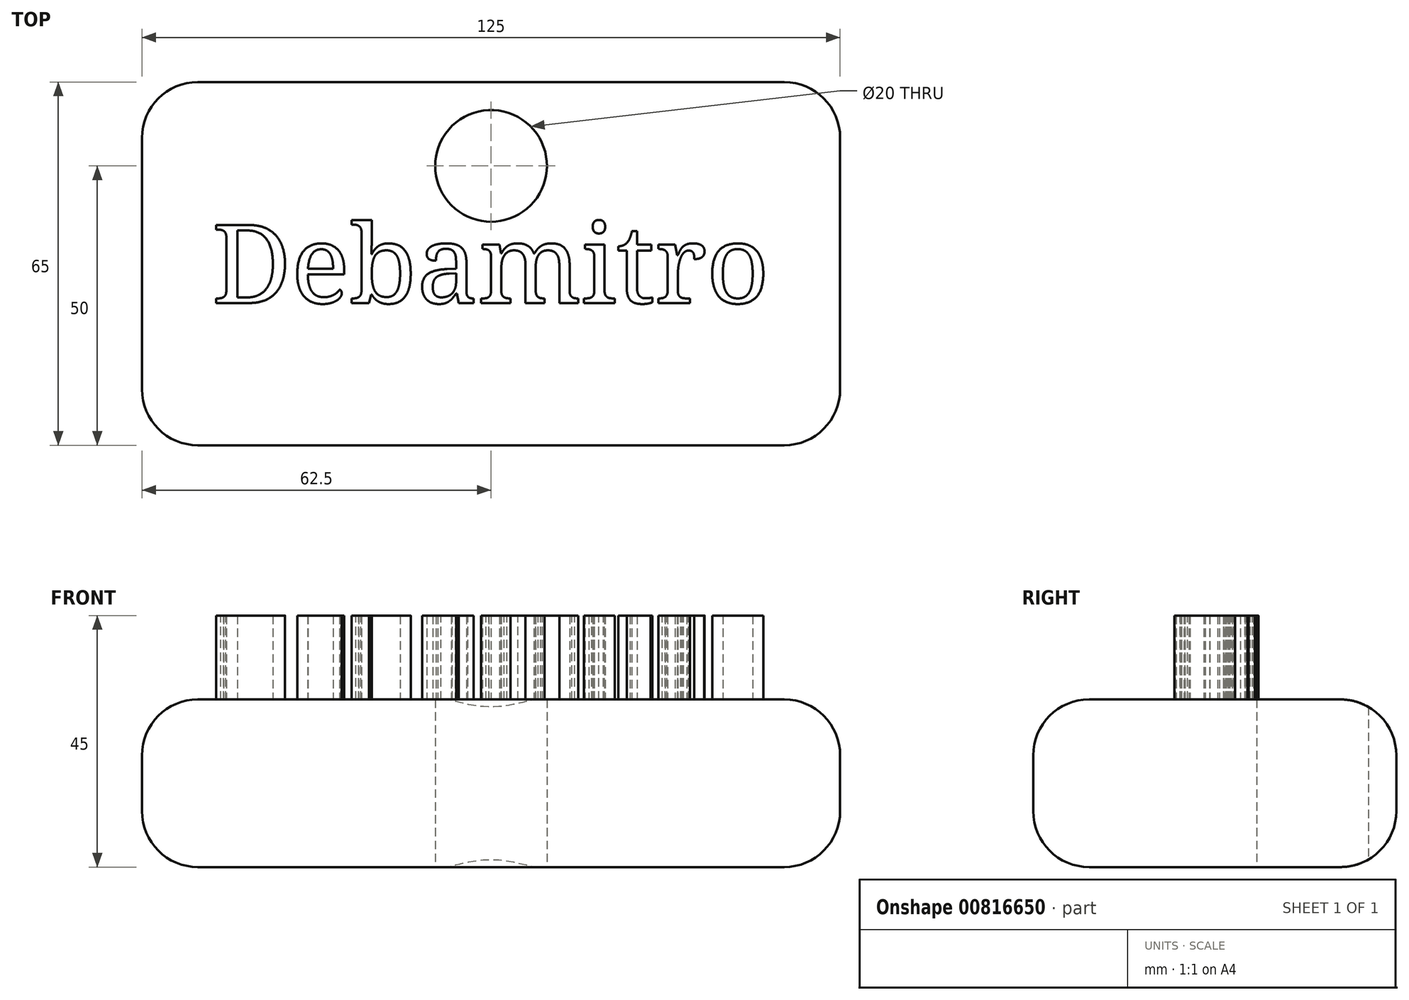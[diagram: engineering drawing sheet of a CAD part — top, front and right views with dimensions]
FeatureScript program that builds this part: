
annotation { "Feature Type Name" : "Feature", "Feature Type Description" : "" }
export const myFeature = defineFeature(function(context is Context, id is Id, definition is map)
    precondition{}
    {
        {
            var Q0;
            Q0=qCreatedBy(makeId("Top.planeOp"),FACE);
            var sketch = newSketch(context, id + "F0", { "sketchPlane" : qUnion([Q0])});
            skLineSegment(sketch, "E0.bottom", {"start": v(62.5, -32.5) * mm, "end": v(-62.5, -32.5) * mm});
            skLineSegment(sketch, "E0.top", {"start": v(62.5, 32.5) * mm, "end": v(-62.5, 32.5) * mm});
            skLineSegment(sketch, "E0.left", {"start": v(62.5, -32.5) * mm, "end": v(62.5, 32.5) * mm});
            skLineSegment(sketch, "E0.right", {"start": v(-62.5, -32.5) * mm, "end": v(-62.5, 32.5) * mm});
            skPoint(sketch, "E0.middle", {"position": v(0, 0) * mm});
            skSolve(sketch);
        }
        {
            var Q0;
            Q0=makeQuery(id+"F0.imprint","IMPRINT",FACE,{"disambiguationData":[TD([[makeQuery(id+"F0.imprint","IMPRINT",EDGE,{"derivedFrom":sQuery(id+"F0.wireOp",EDGE,"E0.bottom")}),-1.0]])]});
            extrude(context, id + "F1", {"entities" : qUnion([Q0]), "depth" : 30 * mm, "offsetDistance" : 25 * mm});
        }
        {
            var Q0;
            Q0=makeQuery(id+"F1.opExtrude","CAP_FACE",FACE,{"disambiguationData":[OSD([sQuery(id+"F0.wireOp",EDGE,"E0.bottom"),sQuery(id+"F0.wireOp",EDGE,"E0.top"),sQuery(id+"F0.wireOp",EDGE,"E0.left"),sQuery(id+"F0.wireOp",EDGE,"E0.right")])],"isStart":false});
            var sketch = newSketch(context, id + "F2", { "sketchPlane" : qUnion([Q0])});
            skText(sketch, "E1", { "text": "Debamitro", "fontName": "NotoSerif-Regular.ttf"});
            skLineSegment(sketch, "E2", {"start": v(0, 7.04) * mm, "end": v(0, 37.53) * mm, "construction": true});
            skLineSegment(sketch, "E3", {"start": v(-50, 0) * mm, "end": v(-58.74, 0) * mm, "construction": true});
            skLineSegment(sketch, "E4", {"start": v(-58.74, 0) * mm, "end": v(-58.48, 1.44) * mm});
            skLineSegment(sketch, "E5", {"start": v(0, -7.04) * mm, "end": v(0, -32.63) * mm, "construction": true});
            skLineSegment(sketch, "E6", {"start": v(50, 0) * mm, "end": v(63.06, 0) * mm, "construction": true});
            const initialGuessF2  = {"E1": [-0.05, -0.00704, 1, 0, 0.01408]};
            skSetInitialGuess(sketch, initialGuessF2);
            skSolve(sketch);
        }
        {
            var Q0;
            Q0 = qSketchRegion(id + "F2", true);
            extrude(context, id + "F3", {"entities" : qUnion([Q0]), "operationType" : NewBodyOperationType.ADD, "depth" : 15 * mm, "offsetDistance" : 25 * mm});
        }
        {
            var Q0;
            Q0=qCreatedBy(makeId("Top.planeOp"),FACE);
            var sketch = newSketch(context, id + "F4", { "sketchPlane" : qUnion([Q0])});
            skCircle(sketch, "E7", {"center": v(0, 17.5) * mm, "radius": 10 * mm});
            skLineSegment(sketch, "E8", {"start": v(0, 17.5) * mm, "end": v(0, 17.5) * mm});
            skLineSegment(sketch, "E9", {"start": v(0, 17.5) * mm, "end": v(0, 32.5) * mm});
            skSolve(sketch);
        }
        {
            var Q0;
            Q0 = qSketchRegion(id + "F4", true);
            extrude(context, id + "F5", {"entities" : qUnion([Q0]), "operationType" : NewBodyOperationType.REMOVE, "depth" : 59 * mm, "offsetDistance" : 25 * mm});
        }
        {
            var Q0;
            Q0=makeQuery(id+"F1.opExtrude","CAP_EDGE",EDGE,{"disambiguationData":[OSD([sQuery(id+"F0.wireOp",EDGE,"E0.right")])],"isStart":false});
            var Q1;
            Q1=makeQuery(id+"F1.opExtrude","CAP_EDGE",EDGE,{"disambiguationData":[OSD([sQuery(id+"F0.wireOp",EDGE,"E0.right")])],"isStart":true});
            var Q2;
            Q2=makeQuery(id+"F1.opExtrude","CAP_EDGE",EDGE,{"disambiguationData":[OSD([sQuery(id+"F0.wireOp",EDGE,"E0.top")])],"isStart":false});
            var Q3;
            Q3=makeQuery(id+"F1.opExtrude","CAP_EDGE",EDGE,{"disambiguationData":[OSD([sQuery(id+"F0.wireOp",EDGE,"E0.top")])],"isStart":true});
            var Q4;
            Q4=makeQuery(id+"F1.opExtrude","CAP_EDGE",EDGE,{"disambiguationData":[OSD([sQuery(id+"F0.wireOp",EDGE,"E0.left")])],"isStart":false});
            var Q5;
            Q5=makeQuery(id+"F1.opExtrude","CAP_EDGE",EDGE,{"disambiguationData":[OSD([sQuery(id+"F0.wireOp",EDGE,"E0.bottom")])],"isStart":false});
            var Q6;
            Q6=makeQuery(id+"F1.opExtrude","SWEPT_EDGE",EDGE,{"disambiguationData":[OSD([sQuery(id+"F0.wireOp",EDGE,"E0.bottom"),sQuery(id+"F0.wireOp",EDGE,"E0.right")])]});
            var Q7;
            Q7=makeQuery(id+"F1.opExtrude","SWEPT_EDGE",EDGE,{"disambiguationData":[OSD([sQuery(id+"F0.wireOp",EDGE,"E0.bottom"),sQuery(id+"F0.wireOp",EDGE,"E0.left")])]});
            var Q8;
            Q8=makeQuery(id+"F1.opExtrude","CAP_EDGE",EDGE,{"disambiguationData":[OSD([sQuery(id+"F0.wireOp",EDGE,"E0.left")])],"isStart":true});
            var Q9;
            Q9=makeQuery(id+"F1.opExtrude","CAP_EDGE",EDGE,{"disambiguationData":[OSD([sQuery(id+"F0.wireOp",EDGE,"E0.bottom")])],"isStart":true});
            var Q10;
            Q10=makeQuery(id+"F1.opExtrude","SWEPT_EDGE",EDGE,{"disambiguationData":[OSD([sQuery(id+"F0.wireOp",EDGE,"E0.top"),sQuery(id+"F0.wireOp",EDGE,"E0.right")])]});
            var Q11;
            Q11=makeQuery(id+"F1.opExtrude","SWEPT_EDGE",EDGE,{"disambiguationData":[OSD([sQuery(id+"F0.wireOp",EDGE,"E0.top"),sQuery(id+"F0.wireOp",EDGE,"E0.left")])]});
            fillet(context, id + "F6", {"entities" : qUnion([Q0, Q1, Q2, Q3, Q4, Q5, Q6, Q7, Q8, Q9, Q10, Q11]), "radius" : 10 * mm, "tangentPropagation" : true, "allowEdgeOverflow" : false});
        }
    });
